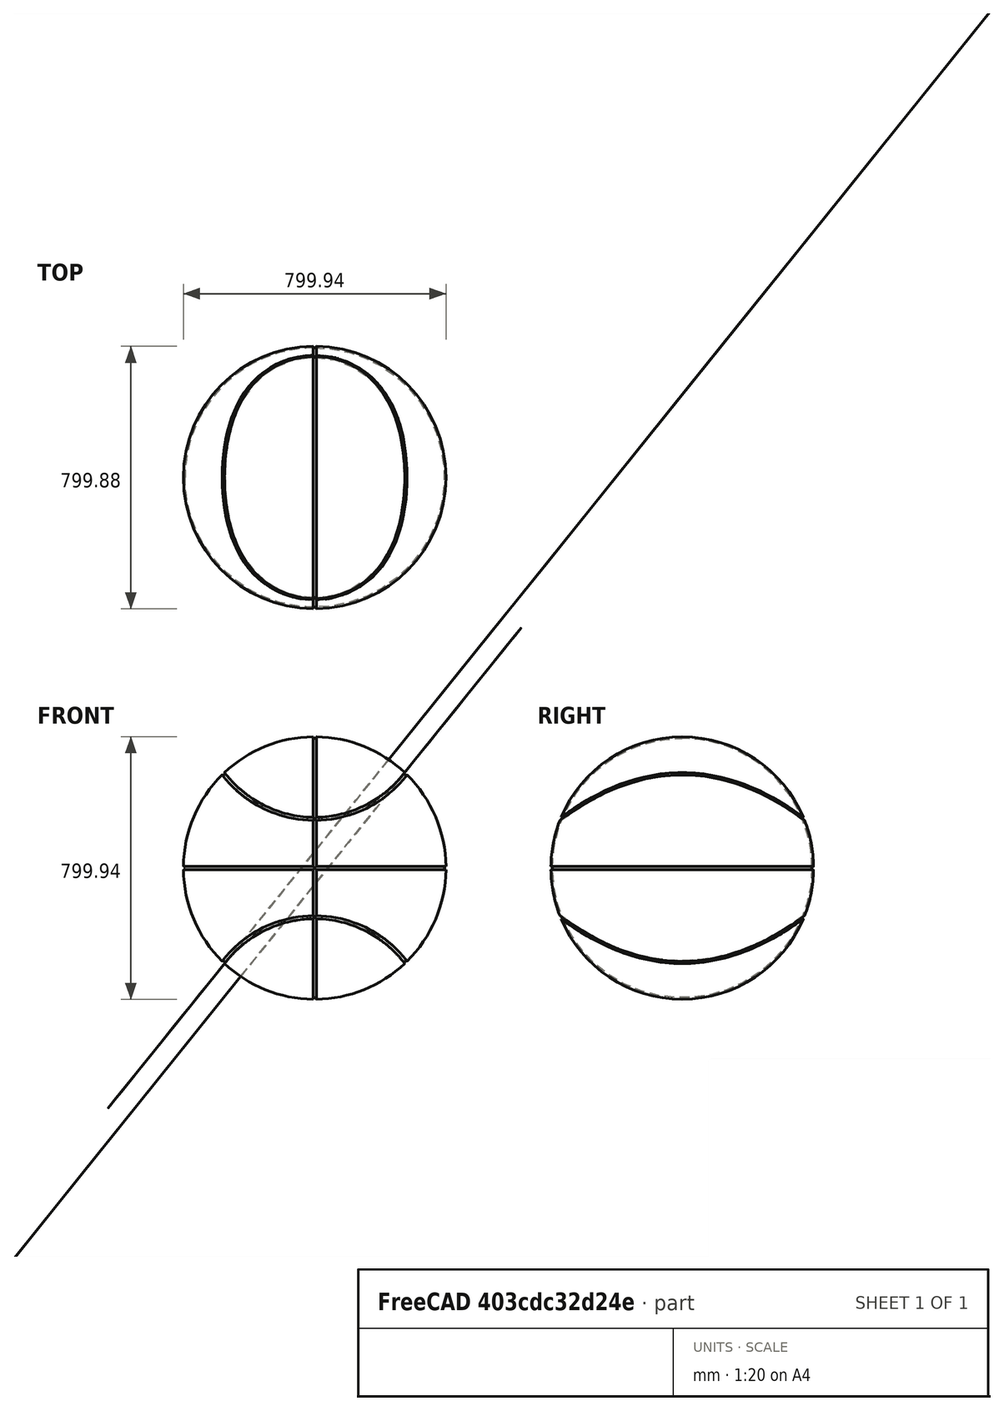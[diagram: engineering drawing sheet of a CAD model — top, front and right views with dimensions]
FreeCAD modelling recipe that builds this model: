
FCSTD DOCUMENT  (FreeCAD 0.18R15419 (Git))
Label: BASKETBALL
License: CreativeCommons Attribution-NonCommercial-ShareAlike
LicenseURL: http://creativecommons.org/licenses/by-nc-sa/4.0/
objects: Part::Sphere×2, Part::Cut×2, Part::FeaturePython×2, Part::Cylinder×1, Part::Circle×1, Part::Sweep×1, Part::Torus×1, Part::MultiFuse×1
note: 11 computed .brp shape members not serialized (recipe doc carries the construction recipe); baked Part::Feature solids carry a one-line shape summary decoded from their .brp

FEATURE [Part::Sphere] Sphere
  Angle1 = -90
  Angle2 = 90
  Angle3 = 360
  AttacherType = Attacher::AttachEngine3D
  Radius = 400
FEATURE [Part::Cylinder] Cylinder
  Angle = 360
  AttacherType = Attacher::AttachEngine3D
  Height = 1000
  Placement = pos=(500,0,-497.11) rot=(0,0,1;0rad)
  Radius = 350
FEATURE [Part::Cut] Cut
  Base = -> Sphere
  Tool = -> Cylinder
FEATURE [Part::Circle] Circle
  Angle0 = 0
  Angle1 = 360
  AttacherType = Attacher::AttachEngine3D
  Placement = pos=(150.01,8.23e-14,370.83) rot=(1,0,0;1.5708rad)
  Radius = 5
FEATURE [Part::Sweep] Sweep
  Frenet = true
  Sections = -> [Circle]
  Solid = true
  Spine = -> Cut [Edge2,Edge5,Edge6]
  Transition = 0
FEATURE [Part::Sphere] Sphere001
  Angle1 = -90
  Angle2 = 90
  Angle3 = 360
  AttacherType = Attacher::AttachEngine3D
  Radius = 400
FEATURE [Part::Torus] Torus
  Angle1 = -180
  Angle2 = 180
  Angle3 = 360
  AttacherType = Attacher::AttachEngine3D
  Placement = pos=(0,0,0) rot=(1,0,0;1.5708rad)
  Radius1 = 400
  Radius2 = 5
FEATURE [Part::FeaturePython] Clone  label="Sweep001"  # Draft clone (typed FeaturePython)
  AttacherType = Attacher::AttachEngine3D
  Fuse = false
  Objects = -> [Sweep]
  Placement = pos=(0,0,0) rot=(0,0,1;3.14159rad)
  Scale = (1,1,1)
FEATURE [Part::FeaturePython] Clone001  label="Torus001"  # Draft clone (typed FeaturePython)
  AttacherType = Attacher::AttachEngine3D
  Fuse = false
  Objects = -> [Torus]
  Placement = pos=(0,0,0) rot=(0.57735,0.57735,0.57735;2.0944rad)
  Scale = (1,1,1)
FEATURE [Part::MultiFuse] Fusion
  Shapes = -> [Clone001,Clone,Torus,Sweep]
FEATURE [Part::Cut] Cut001
  Base = -> Sphere001
  Placement = pos=(0,0,0) rot=(0.57735,-0.57735,0.57735;2.0944rad)
  Tool = -> Fusion
